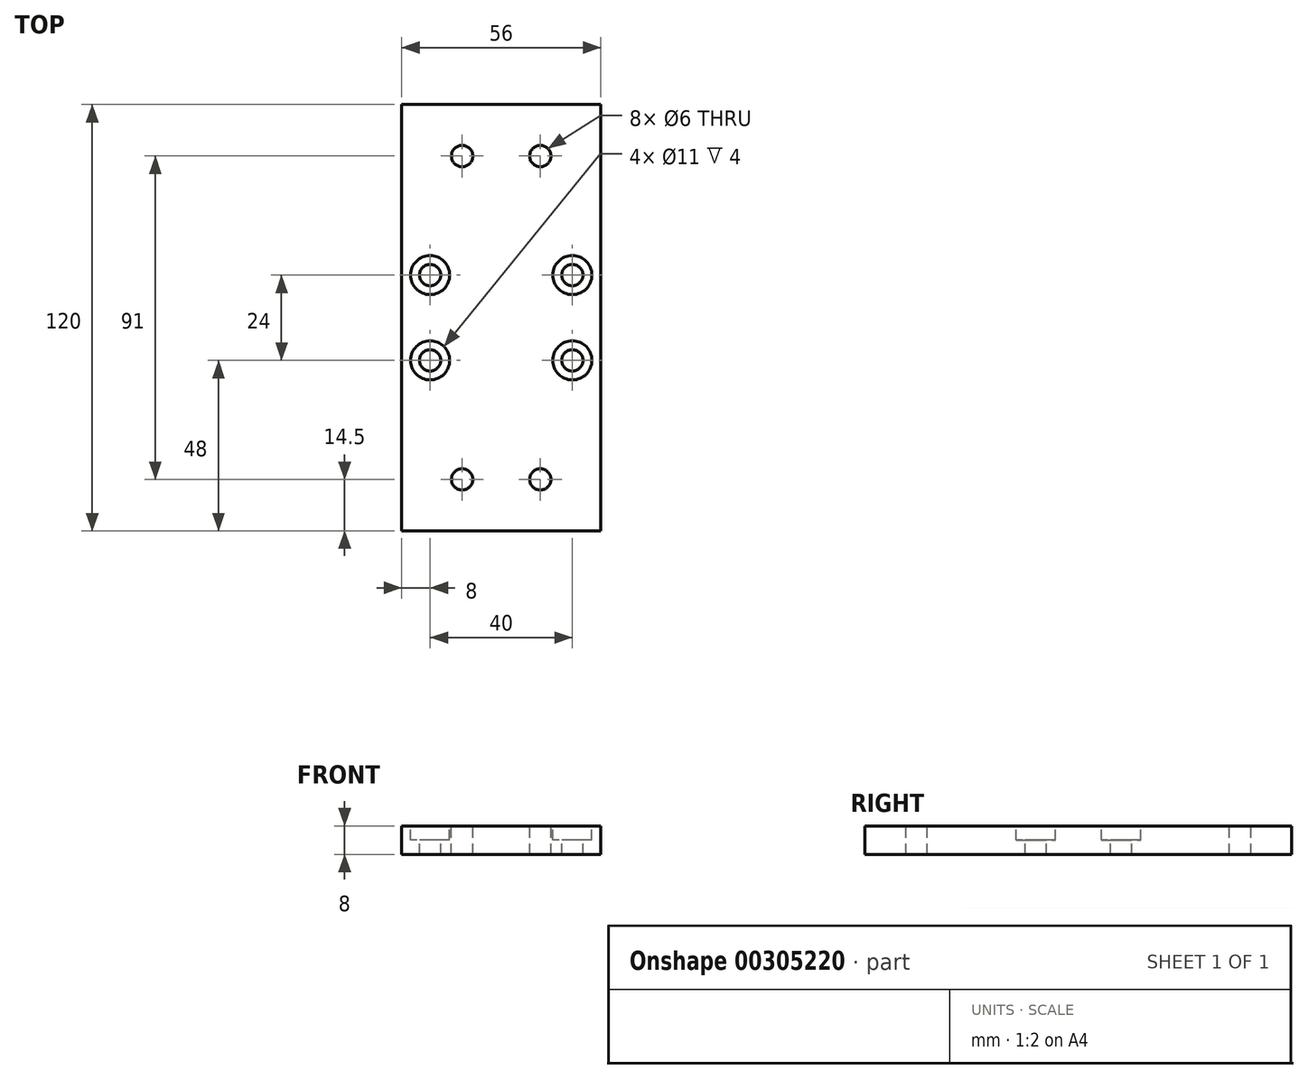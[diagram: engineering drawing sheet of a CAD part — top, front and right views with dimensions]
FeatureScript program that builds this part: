
annotation { "Feature Type Name" : "Feature", "Feature Type Description" : "" }
export const myFeature = defineFeature(function(context is Context, id is Id, definition is map)
    precondition{}
    {
        {
            var Q0;
            Q0=qCreatedBy(makeId("Front.planeOp"),FACE);
            var sketch = newSketch(context, id + "F0", { "sketchPlane" : qUnion([Q0])});
            skLineSegment(sketch, "E0.bottom", {"start": v(0, 0) * mm, "end": v(56, 0) * mm});
            skLineSegment(sketch, "E0.top", {"start": v(0, 8) * mm, "end": v(56, 8) * mm});
            skLineSegment(sketch, "E0.left", {"start": v(0, 0) * mm, "end": v(0, 8) * mm});
            skLineSegment(sketch, "E0.right", {"start": v(56, 0) * mm, "end": v(56, 8) * mm});
            skSolve(sketch);
        }
        {
            var Q0;
            Q0=makeQuery(id+"F0.imprint","IMPRINT",FACE,{"disambiguationData":[TD([[makeQuery(id+"F0.imprint","IMPRINT",EDGE,{"derivedFrom":sQuery(id+"F0.wireOp",EDGE,"E0.bottom")}),1.0]])]});
            extrude(context, id + "F1", {"entities" : qUnion([Q0]), "depth" : 120 * mm});
        }
        {
            var Q0;
            Q0=makeQuery(id+"F1.opExtrude","SWEPT_FACE",FACE,{"disambiguationData":[OSD([sQuery(id+"F0.wireOp",EDGE,"E0.top")])]});
            var sketch = newSketch(context, id + "F2", { "sketchPlane" : qUnion([Q0])});
            skPoint(sketch, "E1", {"position": v(17, -14.5) * mm});
            skPoint(sketch, "E2", {"position": v(39, -14.5) * mm});
            skPoint(sketch, "E3", {"position": v(39, -105.5) * mm});
            skPoint(sketch, "E4", {"position": v(17, -105.5) * mm});
            skSolve(sketch);
        }
        {
            var Q0;
            Q0=sQuery(id+"F2.wireOp",VERTEX,"E1");
            var Q1;
            Q1=sQuery(id+"F2.wireOp",VERTEX,"E2");
            var Q2;
            Q2=sQuery(id+"F2.wireOp",VERTEX,"E4");
            var Q3;
            Q3=sQuery(id+"F2.wireOp",VERTEX,"E3");
            var Q4;
            Q4=makeQuery(id+"F1.opExtrude","SWEPT_BODY",BODY,{"disambiguationData":[OSD([sQuery(id+"F0.wireOp",EDGE,"E0.bottom"),sQuery(id+"F0.wireOp",EDGE,"E0.top"),sQuery(id+"F0.wireOp",EDGE,"E0.left"),sQuery(id+"F0.wireOp",EDGE,"E0.right")])]});
            hole(context, id + "F3", {"style" : HoleStyle.SIMPLE, "endStyle" : HoleEndStyle.THROUGH, "holeDiameter" : 6 * mm, "tappedDepth" : 21 * mm, "tapClearance" : 3, "startFromSketch" : true, "locations" : qUnion([Q0, Q1, Q2, Q3]), "scope" : qUnion([Q4])});
        }
        {
            var Q0;
            Q0=makeQuery(id+"F1.opExtrude","SWEPT_FACE",FACE,{"disambiguationData":[OSD([sQuery(id+"F0.wireOp",EDGE,"E0.top")])]});
            var sketch = newSketch(context, id + "F4", { "sketchPlane" : qUnion([Q0])});
            skPoint(sketch, "E5", {"position": v(8, -48) * mm});
            skPoint(sketch, "E6", {"position": v(48, -48) * mm});
            skPoint(sketch, "E7", {"position": v(48, -72) * mm});
            skPoint(sketch, "E8", {"position": v(8, -72) * mm});
            skPoint(sketch, "E9.endSnap0", {"position": v(56, -60) * mm});
            skSolve(sketch);
        }
        {
            var Q0;
            Q0=sQuery(id+"F4.wireOp",VERTEX,"E5");
            var Q1;
            Q1=sQuery(id+"F4.wireOp",VERTEX,"E8");
            var Q2;
            Q2=sQuery(id+"F4.wireOp",VERTEX,"E6");
            var Q3;
            Q3=sQuery(id+"F4.wireOp",VERTEX,"E7");
            var Q4;
            Q4=makeQuery(id+"F1.opExtrude","SWEPT_BODY",BODY,{"disambiguationData":[OSD([sQuery(id+"F0.wireOp",EDGE,"E0.bottom"),sQuery(id+"F0.wireOp",EDGE,"E0.top"),sQuery(id+"F0.wireOp",EDGE,"E0.left"),sQuery(id+"F0.wireOp",EDGE,"E0.right")])]});
            hole(context, id + "F5", {"style" : HoleStyle.C_BORE, "endStyle" : HoleEndStyle.THROUGH, "standardTappedOrClearance" : lookupTablePath({ "standard" : "ISO", "size" : "6", "type" : "Drilled" }), "standardBlindInLast" : lookupTablePath({ "standard" : "ISO", "size" : "6", "type" : "Drilled" }), "holeDiameter" : 6 * mm, "cBoreDiameter" : 11 * mm, "cBoreDepth" : 4 * mm, "tappedDepth" : 15 * mm, "tapClearance" : 3, "startFromSketch" : true, "locations" : qUnion([Q0, Q1, Q2, Q3]), "scope" : qUnion([Q4])});
        }
    });
